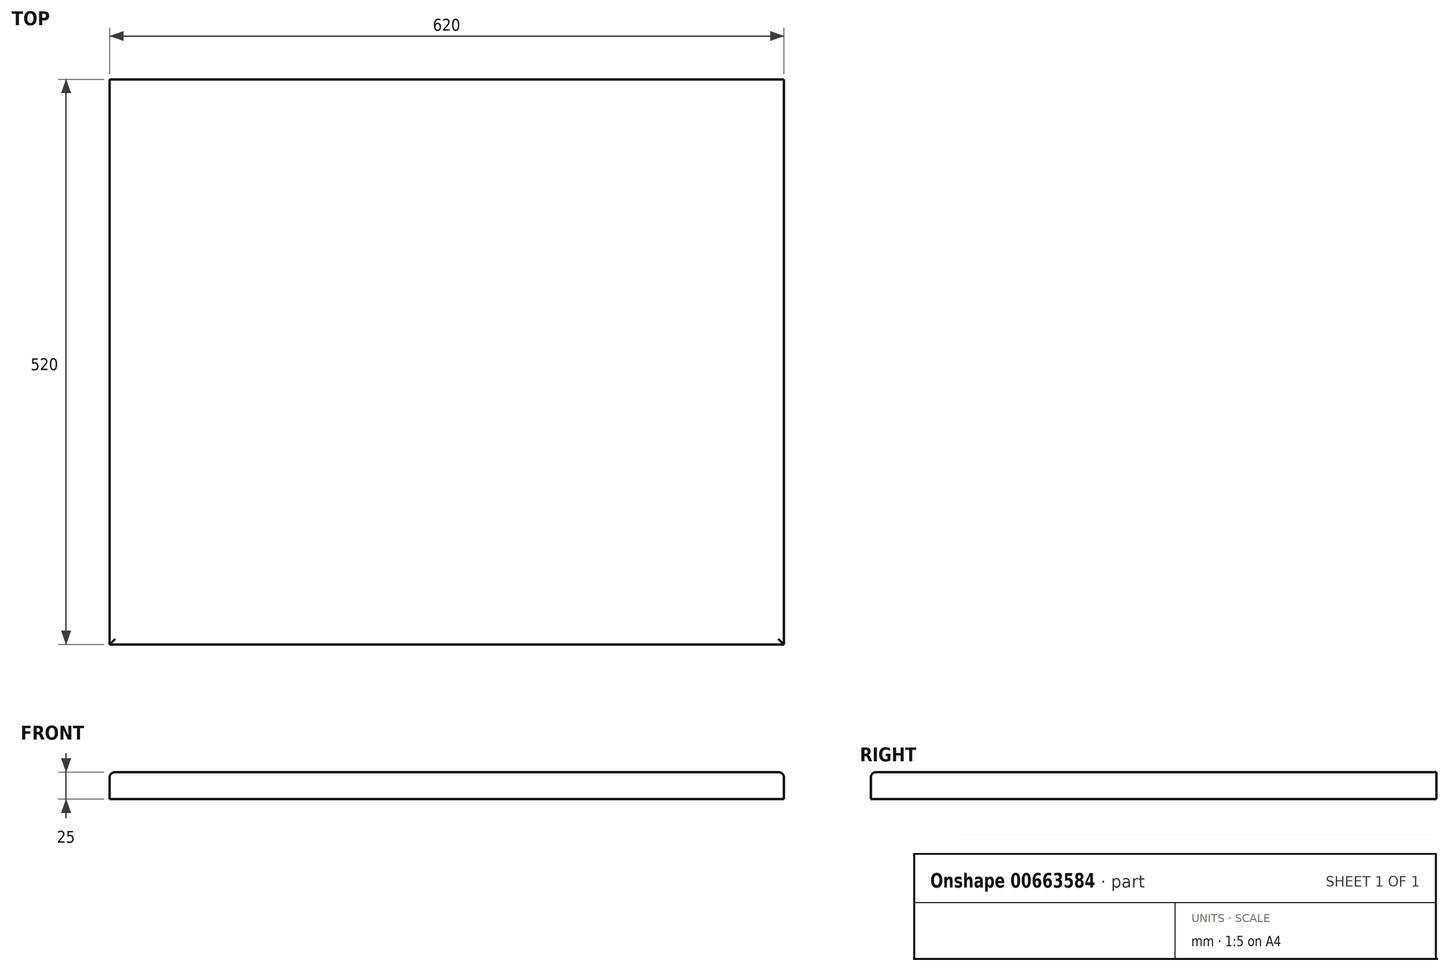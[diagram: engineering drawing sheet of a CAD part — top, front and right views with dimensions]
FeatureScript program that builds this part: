
annotation { "Feature Type Name" : "Feature", "Feature Type Description" : "" }
export const myFeature = defineFeature(function(context is Context, id is Id, definition is map)
    precondition{}
    {
        {
            var Q0;
            Q0=qCreatedBy(makeId("Top.planeOp"),FACE);
            var sketch = newSketch(context, id + "F0", { "sketchPlane" : qUnion([Q0])});
            skLineSegment(sketch, "E0.bottom", {"start": v(310, 260) * mm, "end": v(-310, 260) * mm});
            skLineSegment(sketch, "E0.top", {"start": v(310, -260) * mm, "end": v(-310, -260) * mm});
            skLineSegment(sketch, "E0.left", {"start": v(310, 260) * mm, "end": v(310, -260) * mm});
            skLineSegment(sketch, "E0.right", {"start": v(-310, 260) * mm, "end": v(-310, -260) * mm});
            skPoint(sketch, "E0.middle", {"position": v(0, 0) * mm});
            skSolve(sketch);
        }
        {
            var Q0;
            Q0=makeQuery(id+"F0.imprint","IMPRINT",FACE,{"disambiguationData":[TD([[makeQuery(id+"F0.imprint","IMPRINT",EDGE,{"derivedFrom":sQuery(id+"F0.wireOp",EDGE,"E0.bottom")}),1.0]])]});
            extrude(context, id + "F1", {"entities" : qUnion([Q0]), "depth" : 25 * mm, "offsetDistance" : 25 * mm});
        }
        {
            var Q0;
            Q0=makeQuery(id+"F1.opExtrude","CAP_EDGE",EDGE,{"disambiguationData":[OSD([sQuery(id+"F0.wireOp",EDGE,"E0.top")])],"isStart":false});
            var Q1;
            Q1=makeQuery(id+"F1.opExtrude","CAP_EDGE",EDGE,{"disambiguationData":[OSD([sQuery(id+"F0.wireOp",EDGE,"E0.right")])],"isStart":false});
            var Q2;
            Q2=makeQuery(id+"F1.opExtrude","CAP_EDGE",EDGE,{"disambiguationData":[OSD([sQuery(id+"F0.wireOp",EDGE,"E0.left")])],"isStart":false});
            fillet(context, id + "F2", {"entities" : qUnion([Q0, Q1, Q2]), "radius" : 5 * mm, "tangentPropagation" : true, "allowEdgeOverflow" : false});
        }
    });
